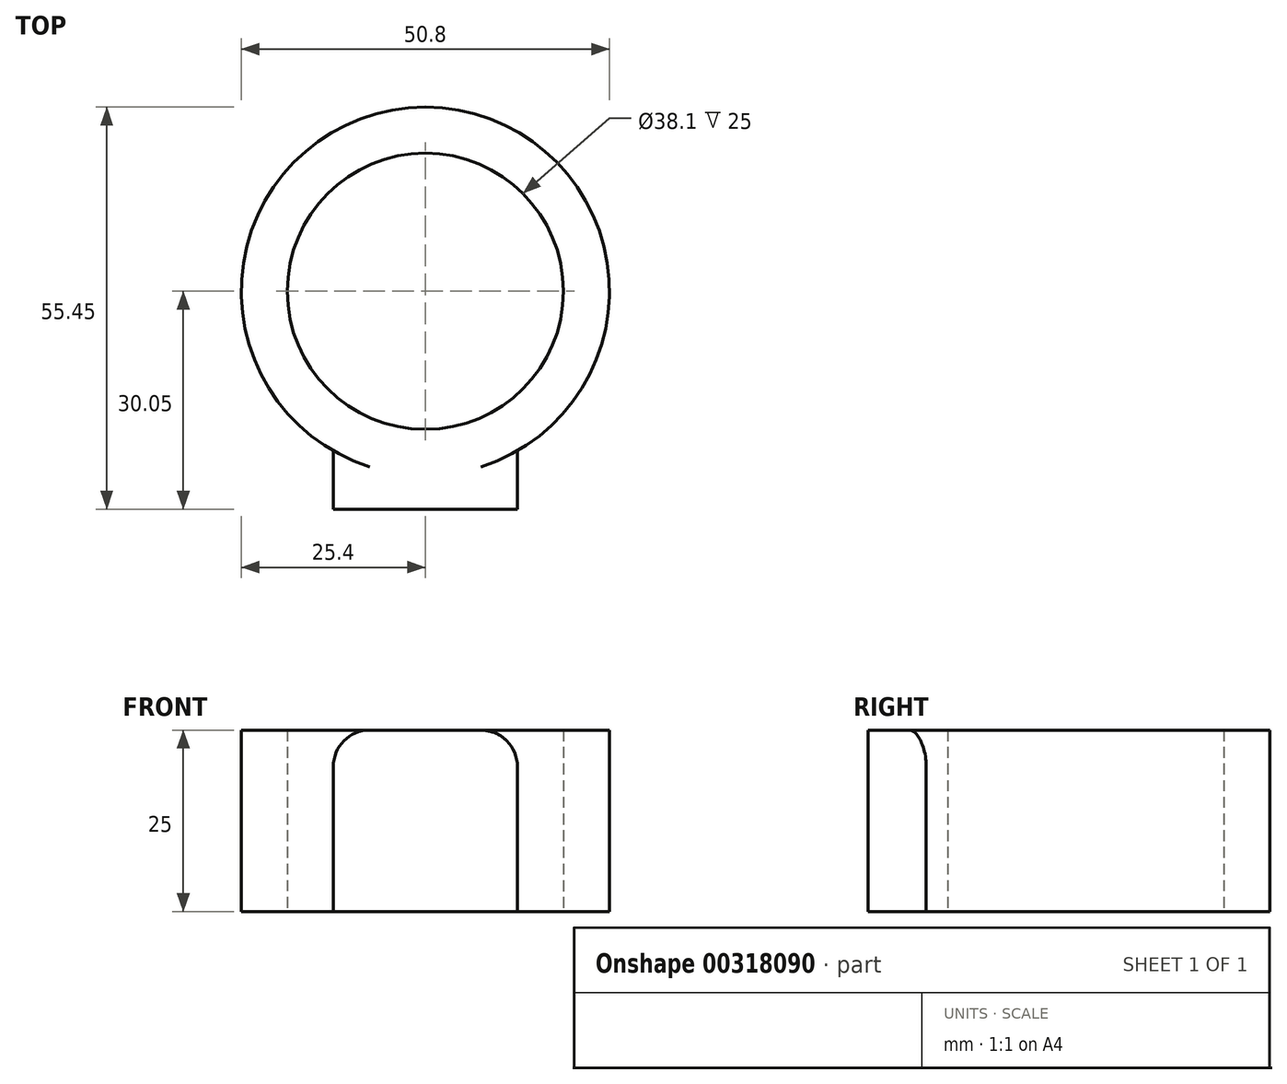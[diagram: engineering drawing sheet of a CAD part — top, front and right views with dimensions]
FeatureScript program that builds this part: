
annotation { "Feature Type Name" : "Feature", "Feature Type Description" : "" }
export const myFeature = defineFeature(function(context is Context, id is Id, definition is map)
    precondition{}
    {
        {
            var Q0;
            Q0=qCreatedBy(makeId("Top.planeOp"),FACE);
            cPlane(context, id + "F0", {"entities" : qUnion([Q0]), "cplaneType" : CPlaneType.OFFSET, "offset" : 38.1 * mm, "width" : 152.4 * mm, "height" : 152.4 * mm});
        }
        {
            var Q0;
            Q0=qCreatedBy(id+"F0.planeOp",FACE);
            var sketch = newSketch(context, id + "F1", { "sketchPlane" : qUnion([Q0])});
            skCircle(sketch, "E0.0", {"center": v(0, 0) * mm, "radius": 19.05 * mm});
            skCircle(sketch, "E0.1", {"center": v(0, 0) * mm, "radius": 25.4 * mm});
            skLineSegment(sketch, "E0.2", {"start": v(-12.7, -22) * mm, "end": v(-12.7, -30.05) * mm});
            skLineSegment(sketch, "E0.3", {"start": v(12.7, -30.05) * mm, "end": v(12.7, -22) * mm});
            skLineSegment(sketch, "E1", {"start": v(-12.7, -30.05) * mm, "end": v(12.7, -30.05) * mm});
            skSolve(sketch);
        }
        {
            var Q0;
            Q0 = qSketchRegion(id + "F1", true);
            extrude(context, id + "F2", {"entities" : qUnion([Q0]), "depth" : 25 * mm});
        }
        {
            var Q0;
            Q0=makeQuery(id+"F2.opExtrude","CAP_EDGE",EDGE,{"disambiguationData":[OSD([sQuery(id+"F1.wireOp",EDGE,"E0.2")])],"isStart":false});
            var Q1;
            Q1=makeQuery(id+"F2.opExtrude","CAP_EDGE",EDGE,{"disambiguationData":[OSD([sQuery(id+"F1.wireOp",EDGE,"E0.3")])],"isStart":false});
            fillet(context, id + "F3", {"entities" : qUnion([Q0, Q1]), "radius" : 5 * mm, "tangentPropagation" : true, "allowEdgeOverflow" : false});
        }
    });
